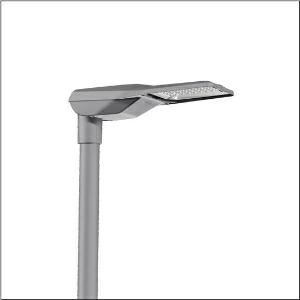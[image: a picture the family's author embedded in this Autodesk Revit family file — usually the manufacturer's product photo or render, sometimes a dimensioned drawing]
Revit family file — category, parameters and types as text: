
# Revit family: streetlight_sl_21_iq_mini___p1_0a_5xe2a31g08hb_5d57
name_source: partatom
category: Lighting Fixtures
units: mm (PartAtom-declared; Revit-internal decimal feet)

## family parameters
Cut with Voids When Loaded = No
Host = Face
Light Source = No
Part Type = Normal
Room Calculation Point = No
Round Connector Dimension = Use Diameter
Shared = No

## types (1)
- --- (1 x LED, 9450 lm, 70.9 W, 3000K)
    Apparent Load = 71 VA
    CIE Flux Codes = 21 50 90 100 100
    Color Rendering = 70
    Color Temperature = 3000K
    Default Elevation = 1800 mm
    Description = Streetlight SL 21 iQ mini, mast luminaire, primary light control with lens, of PMMA, primary optical cover: cover, of toughened safety glass, transparent, light distribution: P1.0a, light emission: direct distribution, primary light characteristic: asymmetric, installation type: post-top, side-entry, LED, High Power LED, rated luminous flux: 9.450lm, luminous efficacy: 133lm/W, light colour: 730, colour temperature: 3000K, control: Street-Remote, Auto-Match, Temp-Guard, Lumen-Switch, Night-Set, Smart-Wire, Light-Fading, Desk-Remote (wireless, voltage-free reading and setting of iQ features in the workshop via application-optimized NFC function/RFID function), optimised constant luminous flux control (CLO 2.0), presetting dimming linear, mains connection: 220..240V, AC, 50/60Hz, start of lifetime: 71W, end of service life: 75W, reduction: 31W, luminaire housing, of diecast aluminium, powder-coated, Siteco® metallic grey (DB 702S), corrosivity category C5 mid according to DIN EN ISO 12944, please order mast flange separately, inclination adjustable: 0°, 5°, 10°, 15°, sealing non-destructively replaceable, multi-level sealing system, length: 628mm, width: 235mm, height: 110mm, mast flange for spigot size: 42mm (side-entry): 5XC10008XM4, 60/48mm (side-entry/post-top): 5XC10108XM2, 76/60mm (side-entry/post-top): 5XC10108XM1, protection rating (complete): IP66, insulation class (complete): insulation class II (safety insulation), certification: CE, ENEC, ENEC+, VDE, impact resistance: IK09, permissible operating ambient temperature for outdoor applications: -40..+50°C, standard-compliant lighting for roads and squares, packaging unit: 1 piece

Light Distribution: P1.0a
    Height = 110 mm
    Lamp = 1 x LED
    Lamp Light Flux = 9450 lm
    Lamp Power = 70.9 W
    Lamp count = 1
    Length = 625 mm
    Luminous efficacy = 133 lm/W
    Manufacturer = Siteco
    ModVariant = No
    Model = 5XE2A31G08HB
    Number of Poles = 1
    OnlyDefault = Yes
    Power Factor = 1
    Product Name = Streetlight SL 21 iQ mini | P1.0a
    Product group = mast luminaire | pylon top
    ProductGroupID = 6100
    Protection Class = Protection class II
    Protection Degree = IP 66
    RLX_Detail_Level = 1
    RLX_Emergency_Light_Flux = 0 lm
    RLX_Emergency_Type = 0
    RLX_Emergency_Type_DB = No
    RlxData = <blob elided: 103449 chars, md5=3356d848>
    Socket = socket
    Standby Power = 0 W
    System Light Flux = 9450 lm
    System Power = 71 W
    Type Comments = factory setting: luminous flux: 100 % | dim-lin: 254 | 711 mA
    Type Image = l_1003519.jpg
    URL = http://relux.com
    VarID = @adj_090001
    Voltage = 0 V
    Weight = 0.00 kg
    Width = 234 mm

## geometry (parser evidence)
native form markers: Blend x4, Sweep x10
no freeform markers — native parametric forms only
